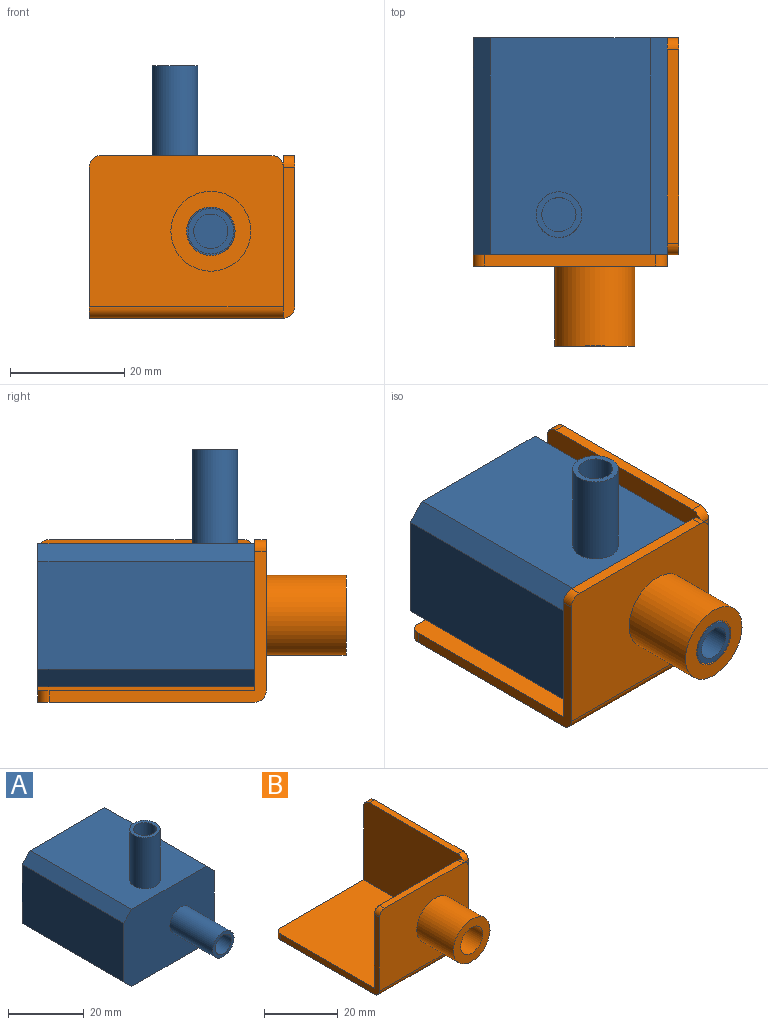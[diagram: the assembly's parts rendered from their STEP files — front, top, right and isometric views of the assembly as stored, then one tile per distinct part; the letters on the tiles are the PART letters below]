
ASSEMBLY  parts=2 mates=1
PART A: 18 faces, bbox 34x54x41.5 mm
  f0: plane 38x19mm, normal (-1,0,0), area 722mm2, adj f1,f3,f6,f9
  f1: plane 34x25mm, normal (0,-1,0), area 781.7mm2, adj f0,f2,f4,f5,f6,f7,f8,f9
  f2: plane 38x19mm, normal (1,0,0), area 722mm2, adj f1,f3,f7,f8
  f3: plane 34x25mm, normal (0,1,0), area 832mm2, adj f0,f2,f4,f5,f6,f7,f8,f9
  f4: plane 38x28mm, normal (0,0,-1), area 1064mm2, adj f1,f3,f6,f7
  f5: plane 38x28mm, normal (0,0,1), area 1013.7mm2, adj f1,f3,f8,f9,f15
  f6: plane 38x3mm, normal (-0.71,0,-0.71), area 161.2mm2, adj f0,f1,f3,f4
  f7: plane 38x3mm, normal (0.71,0,-0.71), area 161.2mm2, adj f1,f2,f3,f4
  f8: plane 38x3mm, normal (0.71,0,0.71), area 161.2mm2, adj f1,f2,f3,f5
  f9: plane 38x3mm, normal (-0.71,0,0.71), area 161.2mm2, adj f0,f1,f3,f5
  f10: cylinder r=3mm len=16mm, axis (0,1,0), area 301.6mm2, adj f12,f13
  f11: cylinder r=4mm len=16mm, axis (0,1,0), area 402.1mm2, adj f1,f12
  f12: plane 8x8mm, normal (0,-1,0), area 22mm2, adj f10,f11
  f13: plane 6x6mm, normal (0,-1,0), area 28.3mm2, adj f10
  f14: cylinder r=3mm len=16.5mm, axis (0,0,-1), area 311mm2, adj f16,f17
  f15: cylinder r=4mm len=16.5mm, axis (0,0,-1), area 414.7mm2, adj f5,f16
  f16: plane 8x8mm, normal (0,0,1), area 22mm2, adj f14,f15
  f17: plane 6x6mm, normal (0,0,1), area 28.3mm2, adj f14
PART B: 23 faces, bbox 36x54x28.5 mm
  f0: plane 38.1x34mm, normal (0,0,1), area 1291.1mm2, adj f1,f5,f6,f7,f10,f12,f20
  f1: plane 26.5x2mm, normal (1,0,0), area 49.7mm2, adj f0,f3,f9,f10,f19,f22
  f2: plane 30x2mm, normal (0,0,1), area 60mm2, adj f3,f6,f21,f22
  f3: plane 34x26.5mm, normal (0,-1,0), area 745.3mm2, adj f1,f2,f7,f13,f19,f21,f22
  f4: plane 38x34mm, normal (0,0,-1), area 1291.1mm2, adj f5,f7,f16,f19,f20
  f5: plane 34x26.5mm, normal (0,1,0), area 116.1mm2, adj f0,f4,f8,f12,f16,f18,f20
  f6: plane 33.9x26.5mm, normal (0,1,0), area 840mm2, adj f0,f2,f7,f10,f15,f21,f22
  f7: plane 38x26.5mm, normal (-1,0,0), area 124.1mm2, adj f0,f3,f4,f6,f19,f20,f21
  f8: plane 38x26.5mm, normal (1,0,0), area 1005.3mm2, adj f5,f9,f11,f16,f17,f18
  f9: plane 26.5x2mm, normal (0,-1,0), area 52.1mm2, adj f1,f8,f12,f16,f17
  f10: plane 25.12x0.1mm, normal (0.71,0.71,0), area 3.5mm2, adj f0,f1,f6,f22
  f11: plane 34x2mm, normal (0,0,1), area 68mm2, adj f8,f12,f17,f18
  f12: plane 38x26.5mm, normal (-1,0,0), area 1005.3mm2, adj f0,f5,f9,f11,f17,f18
  f13: cylinder r=7mm len=14mm, axis (0,1,0), area 615.8mm2, adj f3,f14
  f14: plane 14x14mm, normal (0,-1,0), area 97.2mm2, adj f13,f15
  f15: cylinder r=4.25mm len=16mm, axis (0,-1,0), area 427.3mm2, adj f6,f14
  f16: cylinder r=2mm len=38mm, axis (0,1,0), area 119.4mm2, adj f4,f5,f8,f9
  f17: cylinder r=2mm len=2mm, axis (1,0,0), area 6.3mm2, adj f8,f9,f11,f12
  f18: cylinder r=2mm len=2mm, axis (1,0,0), area 6.3mm2, adj f5,f8,f11,f12
  f19: cylinder r=2mm len=34mm, axis (-1,0,0), area 106.8mm2, adj f1,f3,f4,f7
  f20: cylinder r=2mm len=2mm, axis (0,0,1), area 6.3mm2, adj f0,f4,f5,f7
  f21: cylinder r=2mm len=2mm, axis (0,-1,0), area 6.3mm2, adj f2,f3,f6,f7
  f22: cylinder r=2mm len=2mm, axis (0,1,0), area 6.2mm2, adj f1,f2,f3,f6,f10
PLACE A t=(-2.92,9.7,18.04)mm
PLACE B t=(-2.92,9.7,-7.71)mm
MATE fastened A.f10 <-> B.f13  axis (0,-1,0) through (18.38,9.7,5.54)mm
